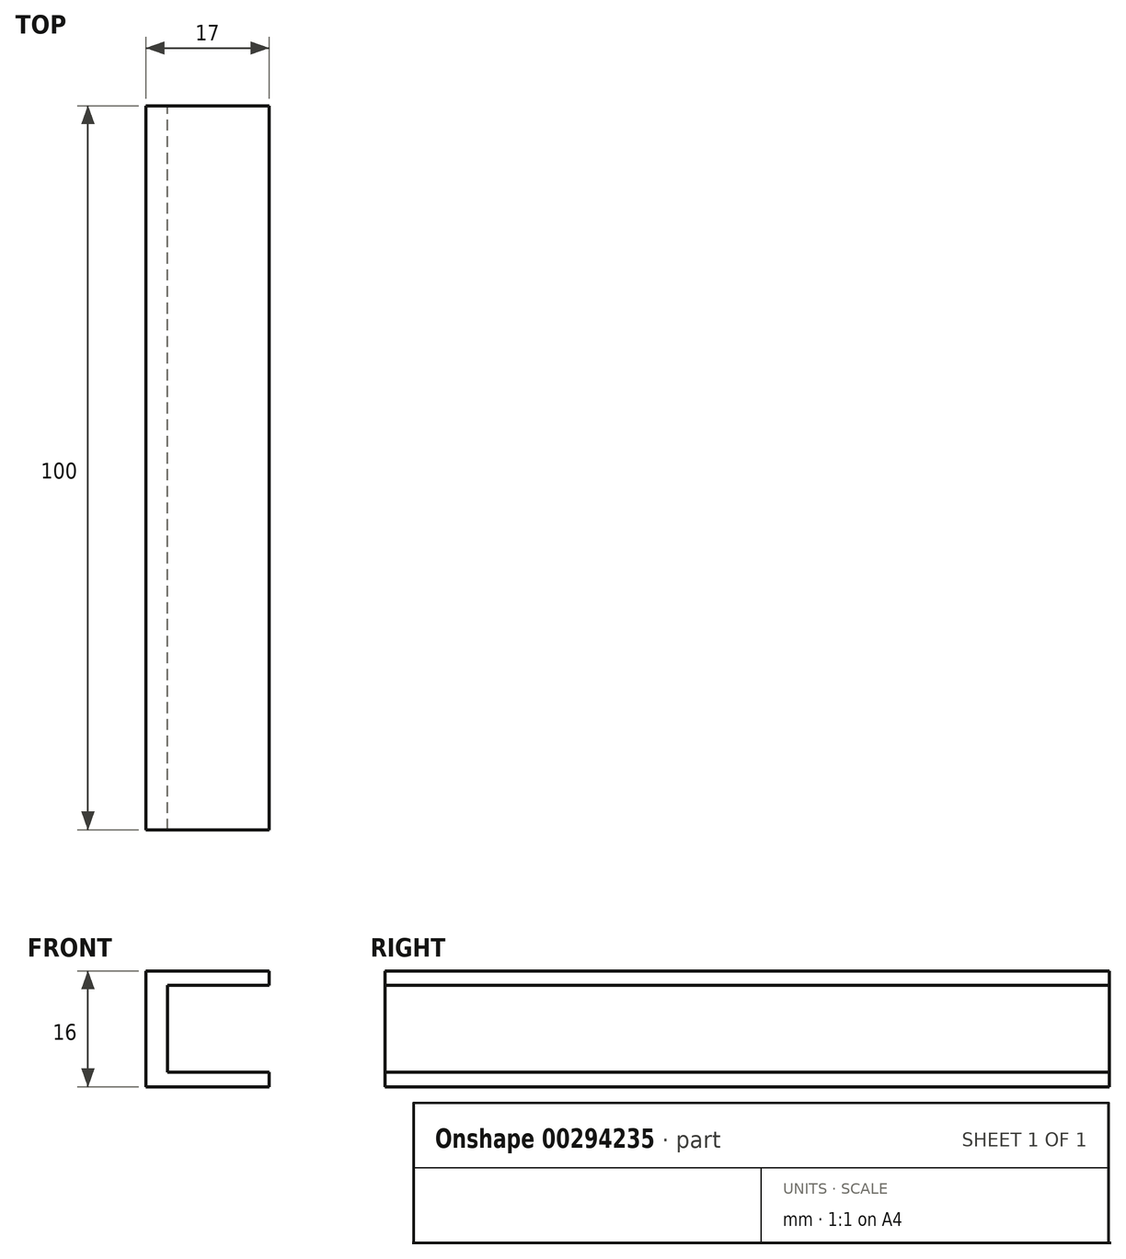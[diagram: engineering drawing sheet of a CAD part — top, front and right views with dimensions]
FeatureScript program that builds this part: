
annotation { "Feature Type Name" : "Feature", "Feature Type Description" : "" }
export const myFeature = defineFeature(function(context is Context, id is Id, definition is map)
    precondition{}
    {
        {
            var Q0;
            Q0=qCreatedBy(makeId("Front.planeOp"),FACE);
            var sketch = newSketch(context, id + "F0", { "sketchPlane" : qUnion([Q0])});
            skLineSegment(sketch, "E0.bottom", {"start": v(0, 0) * mm, "end": v(-17, 0) * mm});
            skLineSegment(sketch, "E0.top", {"start": v(0, 16) * mm, "end": v(-17, 16) * mm});
            skLineSegment(sketch, "E0.left", {"start": v(0, 0) * mm, "end": v(0, 2) * mm});
            skLineSegment(sketch, "E0.right", {"start": v(-17, 0) * mm, "end": v(-17, 16) * mm});
            skLineSegment(sketch, "E1", {"start": v(0, 14) * mm, "end": v(-14, 14) * mm});
            skLineSegment(sketch, "E2", {"start": v(-14, 14) * mm, "end": v(-14, 2) * mm});
            skLineSegment(sketch, "E3", {"start": v(-14, 2) * mm, "end": v(0, 2) * mm});
            skLineSegment(sketch, "E4.trimOffspring", {"start": v(0, 14) * mm, "end": v(0, 16) * mm});
            skSolve(sketch);
        }
        {
            var Q0;
            Q0 = qSketchRegion(id + "F0", true);
            extrude(context, id + "F1", {"entities" : qUnion([Q0]), "depth" : 100 * mm});
        }
    });
